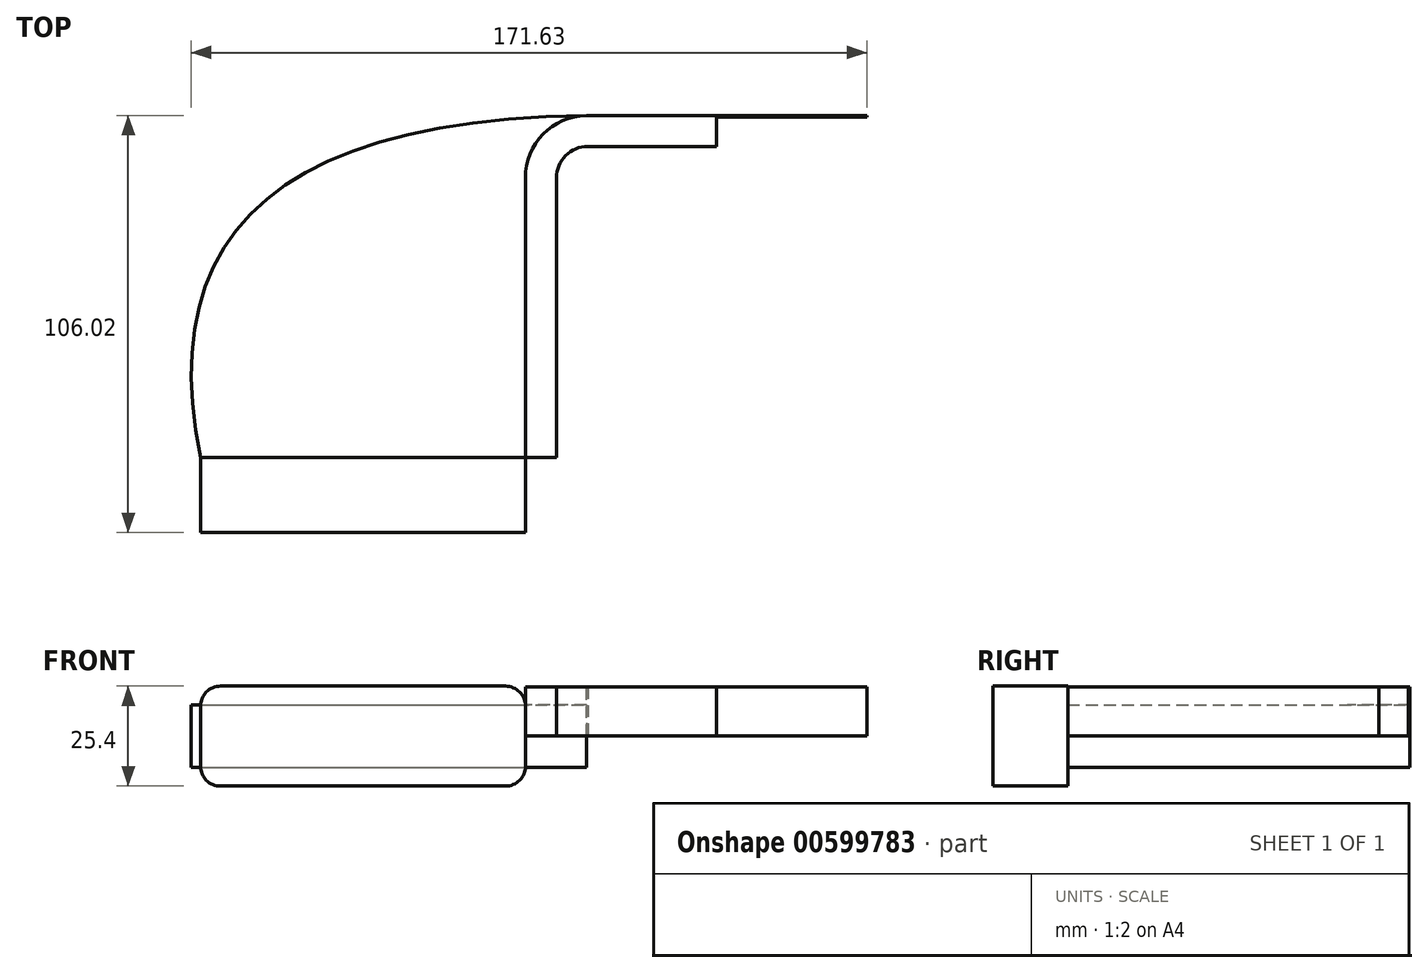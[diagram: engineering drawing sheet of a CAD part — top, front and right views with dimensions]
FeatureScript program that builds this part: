
annotation { "Feature Type Name" : "Feature", "Feature Type Description" : "" }
export const myFeature = defineFeature(function(context is Context, id is Id, definition is map)
    precondition{}
    {
        {
            var Q0;
            Q0=qCreatedBy(makeId("Top.planeOp"),FACE);
            var sketch = newSketch(context, id + "F0", { "sketchPlane" : qUnion([Q0])});
            skLineSegment(sketch, "E0.bottom", {"start": v(-41.28, -9.52) * mm, "end": v(41.28, -9.52) * mm});
            skLineSegment(sketch, "E0.top", {"start": v(-41.28, 9.52) * mm, "end": v(41.27, 9.52) * mm});
            skLineSegment(sketch, "E0.left", {"start": v(-41.27, -9.52) * mm, "end": v(-41.28, 9.52) * mm});
            skLineSegment(sketch, "E0.right", {"start": v(41.28, -9.52) * mm, "end": v(41.27, 9.52) * mm});
            skPoint(sketch, "E0.middle", {"position": v(0, 0) * mm});
            skLineSegment(sketch, "E1.bottom", {"start": v(0, 0) * mm, "end": v(-11.16, 0) * mm});
            skLineSegment(sketch, "E1.top", {"start": v(0, 0) * mm, "end": v(-11.16, 0) * mm});
            skLineSegment(sketch, "E1.left", {"start": v(0, 0) * mm, "end": v(0, 0) * mm});
            skLineSegment(sketch, "E1.right", {"start": v(-11.16, 0) * mm, "end": v(-11.16, 0) * mm});
            skPoint(sketch, "E1.middle", {"position": v(-5.58, 0) * mm});
            skLineSegment(sketch, "E2.bottom", {"start": v(102.62, 64.03) * mm, "end": v(153.42, 64.03) * mm});
            skLineSegment(sketch, "E2.top", {"start": v(102.62, 92.6) * mm, "end": v(153.42, 92.6) * mm});
            skLineSegment(sketch, "E2.left", {"start": v(102.62, 64.03) * mm, "end": v(102.62, 92.6) * mm});
            skLineSegment(sketch, "E2.right", {"start": v(153.42, 64.03) * mm, "end": v(153.42, 92.6) * mm});
            skPoint(sketch, "E2.middle", {"position": v(128.02, 78.32) * mm});
            skLineSegment(sketch, "E3", {"start": v(41.27, 9.52) * mm, "end": v(41.27, 80.61) * mm});
            skArc(sketch, "E4", {"start": v(41.27, 80.61) * mm, "mid": v(45.92, 91.84) * mm, "end": v(57.15, 96.49) * mm});
            skLineSegment(sketch, "E5", {"start": v(57.15, 96.49) * mm, "end": v(128.02, 96.49) * mm});
            skPoint(sketch, "E5.endSnap0", {"position": v(128.02, 64.03) * mm});
            skLineSegment(sketch, "E6.0", {"start": v(57.15, 88.61) * mm, "end": v(128.02, 88.61) * mm});
            skArc(sketch, "E6.1", {"start": v(49.15, 80.61) * mm, "mid": v(51.5, 86.27) * mm, "end": v(57.15, 88.61) * mm});
            skLineSegment(sketch, "E6.2", {"start": v(49.15, 9.52) * mm, "end": v(49.15, 80.61) * mm});
            skLineSegment(sketch, "E7", {"start": v(128.02, 88.61) * mm, "end": v(128.02, 96.49) * mm});
            skLineSegment(sketch, "E8", {"start": v(128.02, 88.61) * mm, "end": v(128.02, 64.03) * mm});
            skFitSpline(sketch, "E9", {"points": [v(-41.28, 9.52) * mm, v(57.15, 96.49) * mm], "startDerivative": vector(-33.98, 166.57) * mm, "endDerivative": vector(241.2, 2.99) * mm});
            skLineSegment(sketch, "E10", {"start": v(41.27, 9.52) * mm, "end": v(49.15, 9.52) * mm});
            skLineSegment(sketch, "E11", {"start": v(128.02, 96.49) * mm, "end": v(128.02, 64.03) * mm});
            skLineSegment(sketch, "E12", {"start": v(128.02, 96.49) * mm, "end": v(197.27, 96.49) * mm});
            skLineSegment(sketch, "E13", {"start": v(197.27, 96.49) * mm, "end": v(197.27, -8.96) * mm});
            skLineSegment(sketch, "E14", {"start": v(197.27, -8.96) * mm, "end": v(41.27, -9.52) * mm});
            skLineSegment(sketch, "E15.bottom", {"start": v(140.62, 57.97) * mm, "end": v(89.82, 57.97) * mm});
            skLineSegment(sketch, "E15.top", {"start": v(140.62, 96.07) * mm, "end": v(89.82, 96.07) * mm});
            skLineSegment(sketch, "E15.left", {"start": v(140.62, 57.97) * mm, "end": v(140.62, 96.07) * mm});
            skLineSegment(sketch, "E15.right", {"start": v(89.82, 57.97) * mm, "end": v(89.82, 96.07) * mm});
            skPoint(sketch, "E15.middle", {"position": v(115.22, 77.02) * mm});
            skSolve(sketch);
        }
        {
            var Q0;
            Q0=makeQuery(id+"F0.imprint","IMPRINT",FACE,{"disambiguationData":[TD([[makeQuery(id+"F0.imprint","IMPRINT",EDGE,{"derivedFrom":sQuery(id+"F0.wireOp",EDGE,"E0.bottom")}),1.0]])]});
            extrude(context, id + "F1", {"entities" : qUnion([Q0]), "endBound" : BoundingType.SYMMETRIC, "depth" : 25.4 * mm, "offsetDistance" : 25.4 * mm});
        }
        {
            var Q0;
            {var subQ9=sQuery(id+"F0.wireOp",EDGE,"E3");Q0=makeQuery(id+"F0.imprint","IMPRINT",FACE,{"disambiguationData":[TD([[makeQuery(id+"F0.imprint","IMPRINT",EDGE,{"derivedFrom":subQ9}),-1.0]])]});}
            extrude(context, id + "F2", {"entities" : qUnion([Q0]), "depth" : 12.45 * mm, "offsetDistance" : 25.4 * mm});
        }
        {
            var Q0;
            {var subQ0=sQuery(id+"F0.wireOp",EDGE,"E0.top");Q0=makeQuery(id+"F0.imprint","IMPRINT",FACE,{"disambiguationData":[TD([[makeQuery(id+"F0.imprint","IMPRINT",EDGE,{"derivedFrom":subQ0}),1.0]])]});}
            extrude(context, id + "F3", {"entities" : qUnion([Q0]), "endBound" : BoundingType.SYMMETRIC, "depth" : 15.88 * mm, "offsetDistance" : 25.4 * mm});
        }
        {
            var Q0;
            Q0=makeQuery(id+"F1.opExtrude","CAP_EDGE",EDGE,{"disambiguationData":[OSD([sQuery(id+"F0.wireOp",EDGE,"E0.right")])],"isStart":false});
            var Q1;
            Q1=makeQuery(id+"F1.opExtrude","CAP_EDGE",EDGE,{"disambiguationData":[OSD([sQuery(id+"F0.wireOp",EDGE,"E0.right")])],"isStart":true});
            var Q2;
            Q2=makeQuery(id+"F1.opExtrude","CAP_EDGE",EDGE,{"disambiguationData":[OSD([sQuery(id+"F0.wireOp",EDGE,"E0.left")])],"isStart":false});
            var Q3;
            Q3=makeQuery(id+"F1.opExtrude","CAP_EDGE",EDGE,{"disambiguationData":[OSD([sQuery(id+"F0.wireOp",EDGE,"E0.left")])],"isStart":true});
            fillet(context, id + "F4", {"entities" : qUnion([Q0, Q1, Q2, Q3]), "radius" : 5.08 * mm, "tangentPropagation" : true, "allowEdgeOverflow" : false});
        }
    });
